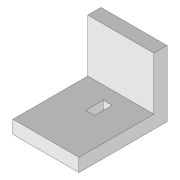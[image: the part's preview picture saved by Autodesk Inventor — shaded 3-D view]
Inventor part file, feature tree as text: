
AUTODESK INVENTOR PART (.ipt)
format: ipt  version: 2020 (Build 240168000, 168)  size: 95,744 bytes
history: native  units: mm
features: extrude x2, sketch x2
ambient origin geometry x8: Origin, YZ Plane, XZ Plane, XY Plane, X Axis, Y Axis, Z Axis, Center Point
bodies: Volumenkörper1 (feature_tree)
feature tree (4):
  extrude  "Extrusion1"  Depth=30.0mm
  extrude  "Extrusion2"  Depth=150.0mm
  sketch  "Skizze2"  dims[d0=30.0mm d1=30.0mm]
  sketch  "Skizze3"  dims[d2=130.0mm d3=150.0mm d4=150.0mm d5=0.0mm d6=150.0mm d7=20.0mm d8=40.0mm d9=65.0mm d10=30.0mm d11=0.0mm d12=0.0mm]
